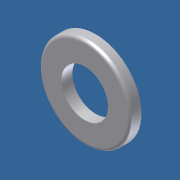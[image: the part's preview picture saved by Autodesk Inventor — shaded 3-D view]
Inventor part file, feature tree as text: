
AUTODESK INVENTOR PART (.ipt)
format: ipt  version: 2012 (Build 160160000, 160)  size: 87,552 bytes
history: native  units: in
note: dims shown in document units (in); Inventor stores cm internally (conversion verified against a paired STEP export)
features: extrude x1, fillet x1, sketch x1
ambient origin geometry x8: Origin, YZ Plane, XZ Plane, XY Plane, X Axis, Y Axis, Z Axis, Center Point
bodies: Solid1 (feature_tree)
feature tree (3):
  extrude  "Extrusion1"  Depth=0.35in
  fillet  "Fillet1"  Radius=0.082in
  sketch  "Sketch1"  dims[d0=0.69in d1=0.35in d2=0.082in d3=0.0in d4=0.025in]
